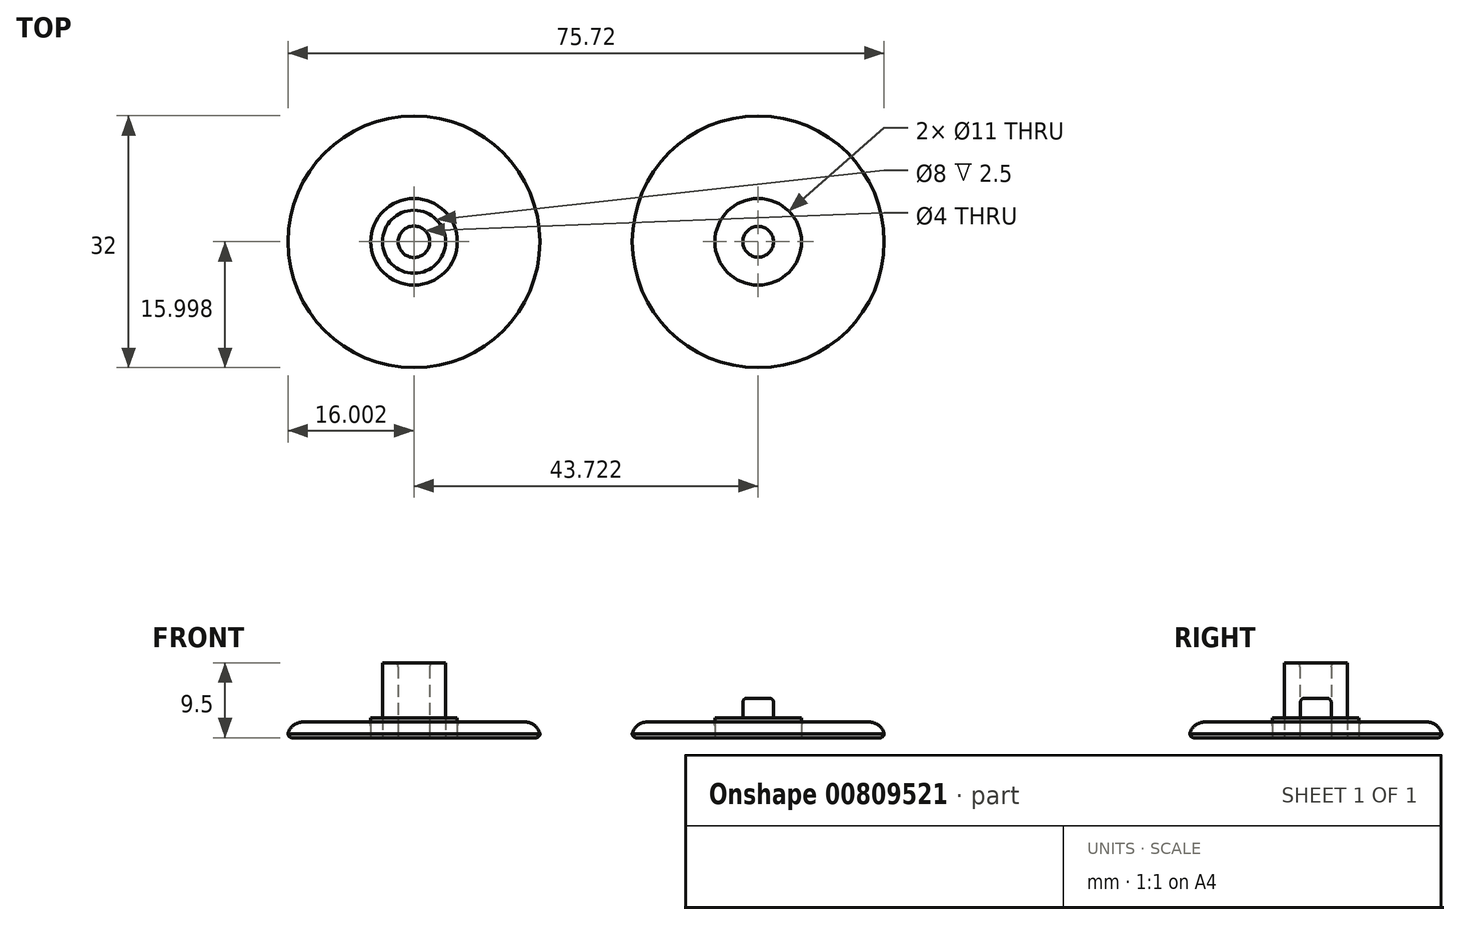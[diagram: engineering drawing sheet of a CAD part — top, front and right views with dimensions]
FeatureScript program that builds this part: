
annotation { "Feature Type Name" : "Feature", "Feature Type Description" : "" }
export const myFeature = defineFeature(function(context is Context, id is Id, definition is map)
    precondition{}
    {
        {
            var Q0;
            Q0=qCreatedBy(makeId("Top.planeOp"),FACE);
            var sketch = newSketch(context, id + "F0", { "sketchPlane" : qUnion([Q0])});
            skCircle(sketch, "E0", {"center": v(-175.6, 134.28) * mm, "radius": 16 * mm});
            skCircle(sketch, "E1", {"center": v(-131.89, 134.28) * mm, "radius": 16 * mm});
            skCircle(sketch, "E2", {"center": v(-175.6, 134.28) * mm, "radius": 5.5 * mm});
            skCircle(sketch, "E3", {"center": v(-175.6, 134.28) * mm, "radius": 4 * mm});
            skCircle(sketch, "E4", {"center": v(-175.6, 134.28) * mm, "radius": 2 * mm});
            skCircle(sketch, "E5", {"center": v(-131.89, 134.28) * mm, "radius": 5.5 * mm});
            skCircle(sketch, "E6", {"center": v(-131.89, 134.28) * mm, "radius": 1.95 * mm});
            skSolve(sketch);
        }
        {
            var Q0;
            Q0=makeQuery(id+"F0.imprint","IMPRINT",FACE,{"disambiguationData":[TD([[makeQuery(id+"F0.imprint","IMPRINT",EDGE,{"derivedFrom":sQuery(id+"F0.wireOp",EDGE,"E0")}),1.0]])]});
            var Q1;
            Q1=makeQuery(id+"F0.imprint","IMPRINT",FACE,{"disambiguationData":[TD([[makeQuery(id+"F0.imprint","IMPRINT",EDGE,{"derivedFrom":sQuery(id+"F0.wireOp",EDGE,"E1")}),1.0]])]});
            extrude(context, id + "F1", {"entities" : qUnion([Q0, Q1]), "depth" : 2 * mm, "offsetDistance" : 25 * mm});
        }
        {
            var Q0;
            Q0=makeQuery(id+"F0.imprint","IMPRINT",FACE,{"disambiguationData":[TD([[makeQuery(id+"F0.imprint","IMPRINT",EDGE,{"derivedFrom":sQuery(id+"F0.wireOp",EDGE,"E2")}),1.0]])]});
            var Q1;
            Q1=makeQuery(id+"F0.imprint","IMPRINT",FACE,{"disambiguationData":[TD([[makeQuery(id+"F0.imprint","IMPRINT",EDGE,{"derivedFrom":sQuery(id+"F0.wireOp",EDGE,"E5")}),1.0]])]});
            var Q2;
            Q2=makeQuery(id+"F0.imprint","IMPRINT",FACE,{"disambiguationData":[TD([[makeQuery(id+"F0.imprint","IMPRINT",EDGE,{"derivedFrom":sQuery(id+"F0.wireOp",EDGE,"E4")}),1.0]])]});
            extrude(context, id + "F2", {"entities" : qUnion([Q0, Q1, Q2]), "depth" : 2.5 * mm, "offsetDistance" : 25 * mm});
        }
        {
            var Q0;
            Q0=makeQuery(id+"F0.imprint","IMPRINT",FACE,{"disambiguationData":[TD([[makeQuery(id+"F0.imprint","IMPRINT",EDGE,{"derivedFrom":sQuery(id+"F0.wireOp",EDGE,"E3")}),1.0]])]});
            extrude(context, id + "F3", {"entities" : qUnion([Q0]), "depth" : 9.5 * mm, "offsetDistance" : 25 * mm});
        }
        {
            var Q0;
            Q0=makeQuery(id+"F0.imprint","IMPRINT",FACE,{"disambiguationData":[TD([[makeQuery(id+"F0.imprint","IMPRINT",EDGE,{"derivedFrom":sQuery(id+"F0.wireOp",EDGE,"E6")}),1.0]])]});
            extrude(context, id + "F4", {"entities" : qUnion([Q0]), "operationType" : NewBodyOperationType.ADD, "depth" : 5 * mm, "offsetDistance" : 25 * mm});
        }
        {
            var Q0;
            Q0=makeQuery(id+"F3.opExtrude","CAP_EDGE",EDGE,{"disambiguationData":[OSD([sQuery(id+"F0.wireOp",EDGE,"E4")])],"isStart":false});
            var Q1;
            Q1=makeQuery(id+"F4.opExtrude","CAP_EDGE",EDGE,{"disambiguationData":[OSD([sQuery(id+"F0.wireOp",EDGE,"E6")])],"isStart":false});
            var Q2;
            Q2=makeQuery(id+"F1.opExtrude","CAP_EDGE",EDGE,{"disambiguationData":[OSD([sQuery(id+"F0.wireOp",EDGE,"E2")])],"isStart":false});
            var Q3;
            Q3=makeQuery(id+"F1.opExtrude","CAP_EDGE",EDGE,{"disambiguationData":[OSD([sQuery(id+"F0.wireOp",EDGE,"E5")])],"isStart":false});
            var Q4;
            Q4=makeQuery(id+"F1.opExtrude","CAP_EDGE",EDGE,{"disambiguationData":[OSD([sQuery(id+"F0.wireOp",EDGE,"E0")])],"isStart":true});
            var Q5;
            Q5=makeQuery(id+"F1.opExtrude","CAP_EDGE",EDGE,{"disambiguationData":[OSD([sQuery(id+"F0.wireOp",EDGE,"E1")])],"isStart":true});
            fillet(context, id + "F5", {"entities" : qUnion([Q0, Q1, Q2, Q3, Q4, Q5]), "radius" : .5 * mm, "tangentPropagation" : true, "allowEdgeOverflow" : false});
        }
        {
            var Q0;
            Q0=makeQuery(id+"F1.opExtrude","CAP_EDGE",EDGE,{"disambiguationData":[OSD([sQuery(id+"F0.wireOp",EDGE,"E0")])],"isStart":false});
            var Q1;
            Q1=makeQuery(id+"F1.opExtrude","CAP_EDGE",EDGE,{"disambiguationData":[OSD([sQuery(id+"F0.wireOp",EDGE,"E1")])],"isStart":false});
            fillet(context, id + "F6", {"entities" : qUnion([Q0, Q1]), "radius" : 2 * mm, "tangentPropagation" : true, "allowEdgeOverflow" : false});
        }
    });
